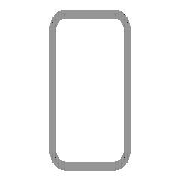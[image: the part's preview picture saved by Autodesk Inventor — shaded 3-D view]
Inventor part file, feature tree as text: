
AUTODESK INVENTOR PART (.ipt)
format: ipt  version: 2025 (Build 290162010, 162A)  size: 131,584 bytes
history: native  units: mm (DEFAULTED — no unit token found)
features: other x4, sketch x1, plane x1
ambient origin geometry x8: Origin, YZ Plane, XZ Plane, XY Plane, X Axis, Y Axis, Z Axis, Center Point
bodies: Solid1 (feature_tree), Body (feature_tree)
feature tree (6):
  parser-record x1  (decoder bookkeeping rows leaked as tree rows — omitted from the tree; the rows remain in map.json)
  other  "Driven Length"
  other  "Start Plane"
  other  "End Plane"
  sketch  "Sketch3"  dims[d3=5400.0mm d4=0.0mm d7=6.0mm d9=40.0mm d11=80.0mm d12=3.0mm d13=-0.0mm d14=5400.0mm d15=20.0mm d16=40.0mm d17=90.0deg d18=5400.0mm]
  plane  "Work Plane3"
